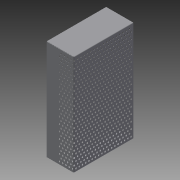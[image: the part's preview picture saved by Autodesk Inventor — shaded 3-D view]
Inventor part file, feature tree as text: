
AUTODESK INVENTOR PART (.ipt)
format: ipt  version: 2015 (Build 190159000, 159)  size: 1,351,680 bytes
history: native  units: mm
features: sheet_metal_op x6, sketch x3, other x2, hole x1
ambient origin geometry x8: Origin, YZ Plane, XZ Plane, XY Plane, X Axis, Y Axis, Z Axis, Center Point
bodies: Body1 (feature_tree)
feature tree (12):
  sketch  "Sketch1"  dims[d0=185.0mm d1=160.0mm]
  sheet_metal_op  "Face5"
  hole  "Hole1"  [1 undecoded]
  sheet_metal_op  "Fold2"
  sheet_metal_op  "Fold3"
  sheet_metal_op  "Flange1"
  other  "Plate5"
  sketch  "Sketch2"  dims[d2=50.0mm]
  sketch  "Sketch3"  dims[d3=0.5mm d9=0.5mm d35=50.0mm d36=230.0mm d38=6.0mm d39=150.0mm d41=12.0mm d44=220.0mm d46=6.0mm d47=150.0mm d49=12.0mm d52=3.0mm d53=6.0mm d54=4.0mm d55=2.0mm d56=90.0deg d57=0.5mm d58=20.594885mm d64=0.5mm d65=0.5mm d66=0.25mm d67=1.0mm d68=0.5mm d69=90.0deg d70=0.5mm d71=0.5mm d72=0.25mm d73=1.0mm d74=0.5mm d75=90.0deg d76=0.5mm d77=0.5mm d78=0.25mm d79=1.0mm d80=0.5mm d81=25.0mm d82=90.0deg d83=0.5mm d84=2.0mm d85=0.5mm d86=0.5mm]
  other  "Plate6"
  sheet_metal_op  "Bend3"
  sheet_metal_op  "Corner1"
note: 1 required parameter value undecoded (feature->parameter linkage not recoverable at this tier; creation-order binding heuristic only, values carry confidence <= 0.55)
